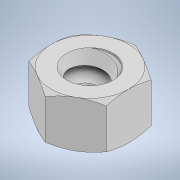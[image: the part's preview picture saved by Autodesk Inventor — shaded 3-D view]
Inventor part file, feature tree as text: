
AUTODESK INVENTOR PART (.ipt)
format: ipt  version: 2021 (Build 250183000, 183)  size: 268,288 bytes
history: native  units: in
note: dims shown in document units (in); Inventor stores cm internally (conversion verified against a paired STEP export)
features: mirror x1
ambient origin geometry x8: Origin, YZ Plane, XZ Plane, XY Plane, X Axis, Y Axis, Z Axis, Center Point
bodies: Solid1 (feature_tree)
feature tree (1):
  mirror  "Mirror1"
